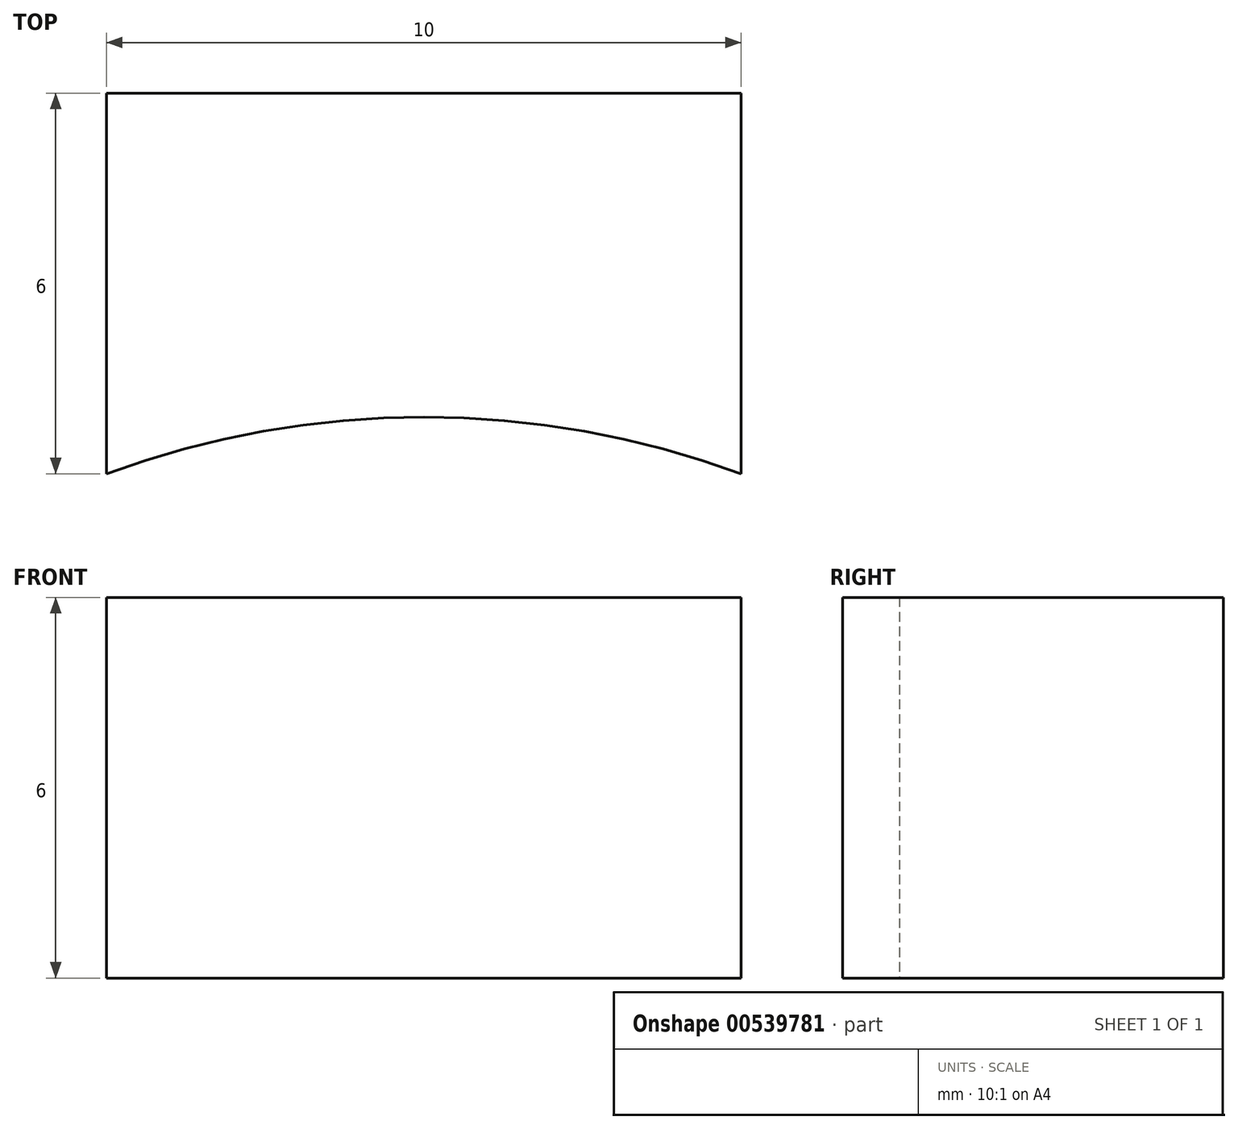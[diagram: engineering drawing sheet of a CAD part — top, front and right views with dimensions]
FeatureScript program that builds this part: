
annotation { "Feature Type Name" : "Feature", "Feature Type Description" : "" }
export const myFeature = defineFeature(function(context is Context, id is Id, definition is map)
    precondition{}
    {
        {
            var Q0;
            Q0=qCreatedBy(makeId("Top.planeOp"),FACE);
            var sketch = newSketch(context, id + "F0", { "sketchPlane" : qUnion([Q0])});
            skLineSegment(sketch, "E0.top", {"start": v(-5, 3) * mm, "end": v(5, 3) * mm});
            skLineSegment(sketch, "E0.left", {"start": v(-5, -3) * mm, "end": v(-5, 3) * mm});
            skLineSegment(sketch, "E0.right", {"start": v(5, -3) * mm, "end": v(5, 3) * mm});
            skPoint(sketch, "E0.middle", {"position": v(0, 0) * mm});
            skArc(sketch, "E1", {"start": v(5, -3) * mm, "mid": v(0, -2.1) * mm, "end": v(-5, -3) * mm});
            skSolve(sketch);
        }
        {
            var Q0;
            Q0 = qSketchRegion(id + "F0", true);
            extrude(context, id + "F1", {"entities" : qUnion([Q0]), "depth" : 6 * mm, "offsetDistance" : 25 * mm});
        }
    });
